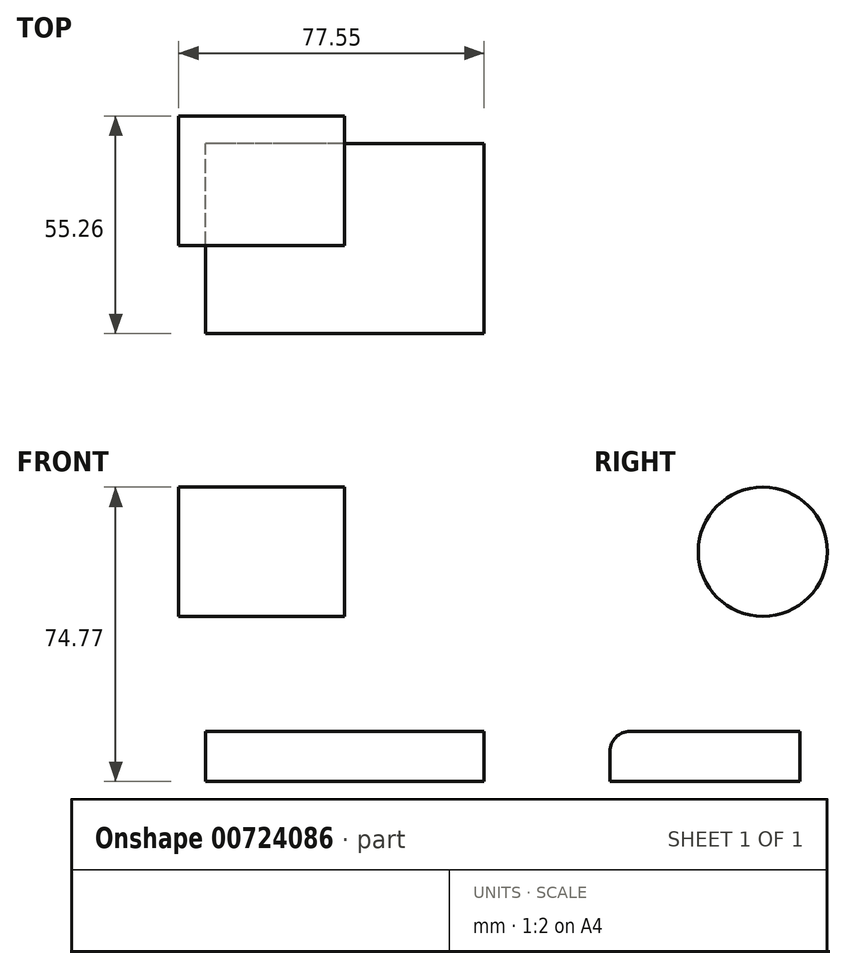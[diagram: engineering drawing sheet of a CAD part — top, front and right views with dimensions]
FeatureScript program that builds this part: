
annotation { "Feature Type Name" : "Feature", "Feature Type Description" : "" }
export const myFeature = defineFeature(function(context is Context, id is Id, definition is map)
    precondition{}
    {
        {
            var Q0;
            Q0=qCreatedBy(makeId("Top.planeOp"),FACE);
            var sketch = newSketch(context, id + "F0", { "sketchPlane" : qUnion([Q0])});
            skLineSegment(sketch, "E0.bottom", {"start": v(35.39, -24.13) * mm, "end": v(-35.39, -24.13) * mm});
            skLineSegment(sketch, "E0.top", {"start": v(35.39, 24.13) * mm, "end": v(-35.39, 24.13) * mm});
            skLineSegment(sketch, "E0.left", {"start": v(35.39, -24.13) * mm, "end": v(35.39, 24.13) * mm});
            skLineSegment(sketch, "E0.right", {"start": v(-35.39, -24.13) * mm, "end": v(-35.39, 24.13) * mm});
            skPoint(sketch, "E0.middle", {"position": v(0, 0) * mm});
            skSolve(sketch);
        }
        {
            var Q0;
            Q0=makeQuery(id+"F0.imprint","IMPRINT",FACE,{"disambiguationData":[TD([[makeQuery(id+"F0.imprint","IMPRINT",EDGE,{"derivedFrom":sQuery(id+"F0.wireOp",EDGE,"E0.bottom")}),-1.0]])]});
            extrude(context, id + "F1", {"entities" : qUnion([Q0]), "depth" : 12.7 * mm, "offsetDistance" : 25.4 * mm});
        }
        {
            var Q0;
            Q0=makeQuery(id+"F1.opExtrude","CAP_EDGE",EDGE,{"disambiguationData":[OSD([sQuery(id+"F0.wireOp",EDGE,"E0.bottom")])],"isStart":false});
            fillet(context, id + "F2", {"entities" : qUnion([Q0]), "radius" : 5.08 * mm, "tangentPropagation" : true, "allowEdgeOverflow" : false});
        }
        {
            var Q0;
            Q0=qCreatedBy(makeId("Right.planeOp"),FACE);
            var sketch = newSketch(context, id + "F3", { "sketchPlane" : qUnion([Q0])});
            skCircle(sketch, "E1", {"center": v(14.72, 58.35) * mm, "radius": 16.42 * mm});
            skSolve(sketch);
        }
        {
            var Q0;
            Q0=makeQuery(id+"F3.imprint","IMPRINT",FACE,{"disambiguationData":[TD([[makeQuery(id+"F3.imprint","IMPRINT",EDGE,{"derivedFrom":sQuery(id+"F3.wireOp",EDGE,"E1")}),1.0]])]});
            extrude(context, id + "F4", {"entities" : qUnion([Q0]), "oppositeDirection" : true, "depth" : 42.16 * mm, "offsetDistance" : 25.4 * mm});
        }
    });
